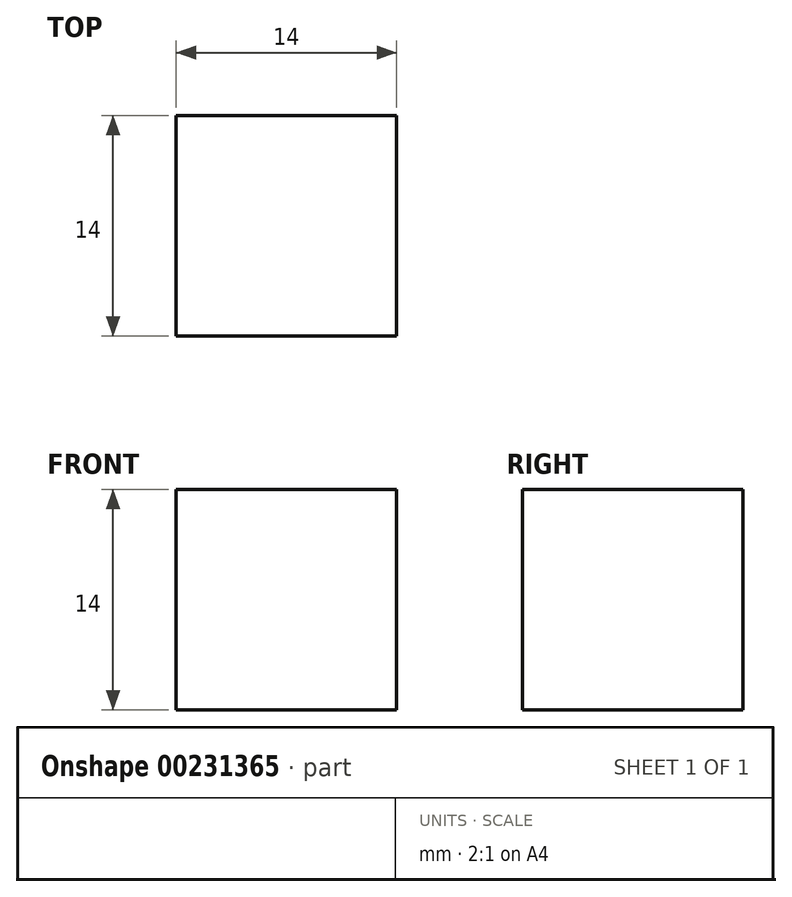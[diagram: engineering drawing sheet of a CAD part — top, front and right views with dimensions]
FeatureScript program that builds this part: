
annotation { "Feature Type Name" : "Feature", "Feature Type Description" : "" }
export const myFeature = defineFeature(function(context is Context, id is Id, definition is map)
    precondition{}
    {
        {
            var Q0;
            Q0=qCreatedBy(makeId("Top.planeOp"),FACE);
            var sketch = newSketch(context, id + "F0", { "sketchPlane" : qUnion([Q0])});
            skLineSegment(sketch, "E0.bottom", {"start": v(7, -7) * mm, "end": v(-7, -7) * mm});
            skLineSegment(sketch, "E0.top", {"start": v(7, 7) * mm, "end": v(-7, 7) * mm});
            skLineSegment(sketch, "E0.left", {"start": v(7, -7) * mm, "end": v(7, 7) * mm});
            skLineSegment(sketch, "E0.right", {"start": v(-7, -7) * mm, "end": v(-7, 7) * mm});
            skPoint(sketch, "E0.middle", {"position": v(0, 0) * mm});
            skSolve(sketch);
        }
        {
            var Q0;
            Q0 = qSketchRegion(id + "F0", true);
            extrude(context, id + "F1", {"entities" : qUnion([Q0]), "depth" : 14 * mm});
        }
    });
